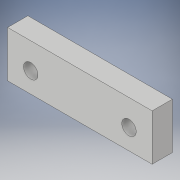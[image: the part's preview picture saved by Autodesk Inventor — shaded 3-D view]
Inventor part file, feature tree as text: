
AUTODESK INVENTOR PART (.ipt)
format: ipt  version: 2017 (Build 210142000, 142)  size: 101,888 bytes
history: native  units: in
note: dims shown in document units (in); Inventor stores cm internally (conversion verified against a paired STEP export)
features: sketch x5, extrude x1, hole x1
ambient origin geometry x8: Origin, YZ Plane, XZ Plane, XY Plane, X Axis, Y Axis, Z Axis, Center Point
bodies: Solid1 (feature_tree)
feature tree (7):
  extrude  "Extrusion1"  Depth=0.6299in
  hole  "Hole1"  [1 undecoded]
  sketch  "Sketch3"  dims[d5=0.2756in]
  sketch  "Sketch4"  dims[d6=1.3386in]
  sketch  "Sketch5"  dims[d7=0.1969in d8=0.2362in d9=0.1575in d10=0.0787in d11=90.0deg d12=0.315in d13=0.8108in d14=0.315in]
  sketch  "Sketch1"  dims[d0=1.9685in d1=0.6299in]
  sketch  "Sketch2"  dims[d2=0.2756in d3=0.0in d4=0.2756in]
note: 1 required parameter value undecoded (feature->parameter linkage not recoverable at this tier; creation-order binding heuristic only, values carry confidence <= 0.55)
